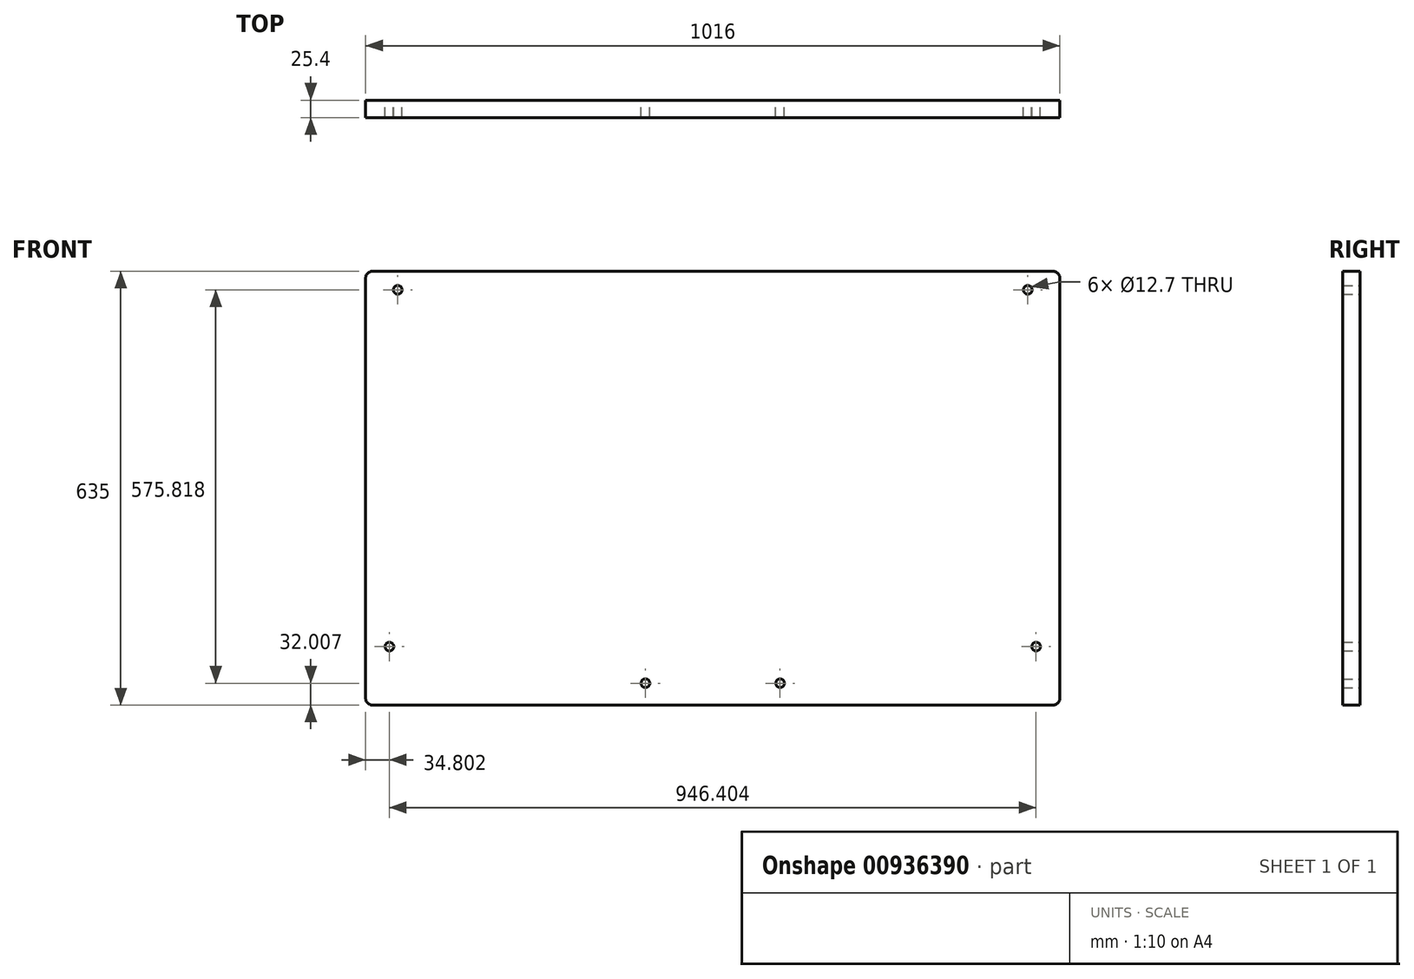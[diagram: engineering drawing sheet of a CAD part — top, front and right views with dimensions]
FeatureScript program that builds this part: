
annotation { "Feature Type Name" : "Feature", "Feature Type Description" : "" }
export const myFeature = defineFeature(function(context is Context, id is Id, definition is map)
    precondition{}
    {
        {
            var Q0;
            Q0=qCreatedBy(makeId("Front.planeOp"),FACE);
            var sketch = newSketch(context, id + "F0", { "sketchPlane" : qUnion([Q0])});
            skLineSegment(sketch, "E0.bottom", {"start": v(-352.98, 352.23) * mm, "end": v(642.7, 352.23) * mm});
            skLineSegment(sketch, "E0.top", {"start": v(-352.98, -282.77) * mm, "end": v(642.7, -282.77) * mm});
            skLineSegment(sketch, "E0.left", {"start": v(-363.14, 342.07) * mm, "end": v(-363.14, -272.6) * mm});
            skLineSegment(sketch, "E0.right", {"start": v(652.86, 342.07) * mm, "end": v(652.86, -272.6) * mm});
            skLineSegment(sketch, "E1", {"start": v(144.86, 352.23) * mm, "end": v(144.86, -282.77) * mm, "construction": true});
            skLineSegment(sketch, "E2", {"start": v(652.86, 199.83) * mm, "end": v(-363.14, 199.83) * mm, "construction": true});
            skCircle(sketch, "E3", {"center": v(-316.15, 325.05) * mm, "radius": 6.35 * mm});
            skCircle(sketch, "E4", {"center": v(-328.34, -197.17) * mm, "radius": 6.35 * mm});
            skCircle(sketch, "E5", {"center": v(46.31, -250.76) * mm, "radius": 6.35 * mm});
            skCircle(sketch, "E6.MirrorC", {"center": v(618.07, -197.17) * mm, "radius": 6.35 * mm});
            skCircle(sketch, "E7.MirrorC", {"center": v(605.87, 325.05) * mm, "radius": 6.35 * mm});
            skCircle(sketch, "E8.MirrorC", {"center": v(243.42, -250.76) * mm, "radius": 6.35 * mm});
            skPoint(sketch, "E9.visualSharp", {"position": v(-363.14, 352.23) * mm});
            skArc(sketch, "E9.filletArc", {"start": v(-352.98, 352.23) * mm, "mid": v(-360.16, 349.26) * mm, "end": v(-363.14, 342.07) * mm});
            skPoint(sketch, "E10.visualSharp", {"position": v(652.86, 352.23) * mm});
            skArc(sketch, "E10.filletArc", {"start": v(652.86, 342.07) * mm, "mid": v(649.89, 349.26) * mm, "end": v(642.7, 352.23) * mm});
            skPoint(sketch, "E11.visualSharp", {"position": v(652.86, -282.77) * mm});
            skArc(sketch, "E11.filletArc", {"start": v(642.7, -282.77) * mm, "mid": v(649.89, -279.8) * mm, "end": v(652.86, -272.6) * mm});
            skPoint(sketch, "E12.visualSharp", {"position": v(-363.14, -282.77) * mm});
            skArc(sketch, "E12.filletArc", {"start": v(-363.14, -272.6) * mm, "mid": v(-360.16, -279.8) * mm, "end": v(-352.98, -282.77) * mm});
            skSolve(sketch);
        }
        {
            var Q0;
            Q0=qSketchRegion(id+"F0",true);
            extrude(context, id + "F1", {"entities" : qUnion([Q0]), "depth" : 25.4 * mm, "offsetDistance" : 25.4 * mm});
        }
    });
